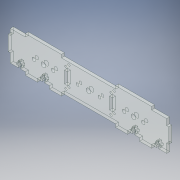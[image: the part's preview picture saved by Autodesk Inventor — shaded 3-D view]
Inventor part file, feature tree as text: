
AUTODESK INVENTOR PART (.ipt)
format: ipt  version: 2019 (Build 230136000, 136)  size: 560,128 bytes
history: native  units: mm
features: projected_geometry x11, extrude x10, sketch x10
ambient origin geometry x8: Origin, YZ Plane, XZ Plane, XY Plane, X Axis, Y Axis, Z Axis, Center Point
bodies: Body1 (feature_tree)
feature tree (31):
  extrude  "Extrusion2"  Depth=8.0mm
  extrude  "Extrusion3"  Depth=8.0mm
  extrude  "Extrusion4"  Depth=5.0mm TaperAngle=0.0deg
  extrude  "Extrusion5"  Depth=5.0mm TaperAngle=0.0deg
  extrude  "Extrusion6"  Depth=5.0mm TaperAngle=0.0deg
  extrude  "Extrusion7"  Depth=40.0mm
  extrude  "Extrusion9"  Depth=20.0mm
  extrude  "Extrusion10"  Depth=5.0mm TaperAngle=0.0deg
  extrude  "Extrusion11"  Depth=5.0mm
  extrude  "Extrusion12"  Depth=5.0mm TaperAngle=0.0deg
  sketch  "Sketch1"  dims[d1=50.0mm d2=5.0mm d3=50.0mm d4=50.0mm d5=50.0mm d6=6.0mm d7=6.0mm d8=32.0mm d9=6.0mm d10=6.0mm d11=32.0mm d12=59.0mm d13=59.0mm d16=8.0mm]
  sketch  "Sketch2"  dims[d17=16.0mm d18=8.0mm]
  sketch  "Sketch3"  dims[d19=16.0mm d20=5.0mm d21=0.0mm]
  projected_geometry  "Projected Loop1"
  projected_geometry  "Projected Loop2"
  sketch  "Sketch4"  dims[d22=8.0mm d23=5.0mm d24=0.0mm]
  projected_geometry  "Projected Loop3"
  projected_geometry  "Projected Loop4"
  projected_geometry  "Projected Loop5"
  sketch  "Sketch5"  dims[d25=5.0mm d26=0.0mm d27=5.0mm d28=0.0mm]
  projected_geometry  "Projected Loop6"
  sketch  "Sketch6"  dims[d29=100.0mm d30=40.0mm]
  projected_geometry  "Projected Loop7"
  sketch  "Sketch8"  dims[d31=40.0mm d32=20.0mm]
  projected_geometry  "Projected Loop9"
  sketch  "Sketch9"  dims[d33=20.0mm d34=5.0mm d35=0.0mm]
  projected_geometry  "Projected Loop10"
  sketch  "Sketch10"  dims[d36=5.0mm d37=5.0mm]
  projected_geometry  "Projected Loop11"
  sketch  "Sketch11"  dims[d38=5.0mm d39=5.0mm d40=0.0mm d43=5.0mm d44=5.0mm d45=5.0mm d46=5.0mm d47=5.0mm d48=0.0mm d49=20.0mm d50=20.0mm d51=20.0mm d52=20.0mm d53=8.0mm d54=4.0mm d55=10.0mm d56=8.0mm d57=4.0mm d58=5.0mm d59=0.0mm d60=5.0mm d61=20.0mm d62=5.0mm d63=20.0mm d64=5.0mm d65=5.0mm d66=4.0mm d67=4.0mm d68=4.0mm d69=4.0mm d70=6.0mm d71=6.0mm d72=6.0mm d73=6.0mm d74=10.0mm d75=0.0mm d76=3.5mm d77=25.0mm d78=10.0mm d79=5.0mm d80=0.0mm]
  projected_geometry  "Projected Loop12"
